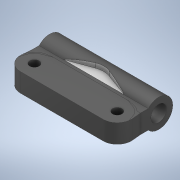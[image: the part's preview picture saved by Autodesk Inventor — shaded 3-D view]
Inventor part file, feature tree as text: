
AUTODESK INVENTOR PART (.ipt)
format: ipt  version: 2020 (Build 240168000, 168)  size: 231,424 bytes
history: native  units: in
note: dims shown in document units (in); Inventor stores cm internally (conversion verified against a paired STEP export)
features: other x4, extrude x2, sketch x2, projected_geometry x2
ambient origin geometry x8: Origin, YZ Plane, XZ Plane, XY Plane, X Axis, Y Axis, Z Axis, Center Point
bodies: Solid1 (feature_tree)
feature tree (10):
  other  "prog to kauri rear link mod.iam"
  other  "399 prig z plate.ipt:1"
  other  "399 prig z plate.ipt:2"
  other  "KauriRearLink 35mm no brass insert.ipt:1"
  extrude  "Extrusion1"  Depth=0.3937in
  extrude  "Extrusion2"  Depth=0.3937in
  sketch  "Sketch1"  dims[d0=0.3937in d1=0.0079in]
  projected_geometry  "Projected Loop1"
  sketch  "Sketch2"  dims[d2=0.3937in d3=0.0in d4=0.0079in d5=0.3937in d6=0.0in]
  projected_geometry  "Projected Loop2"
